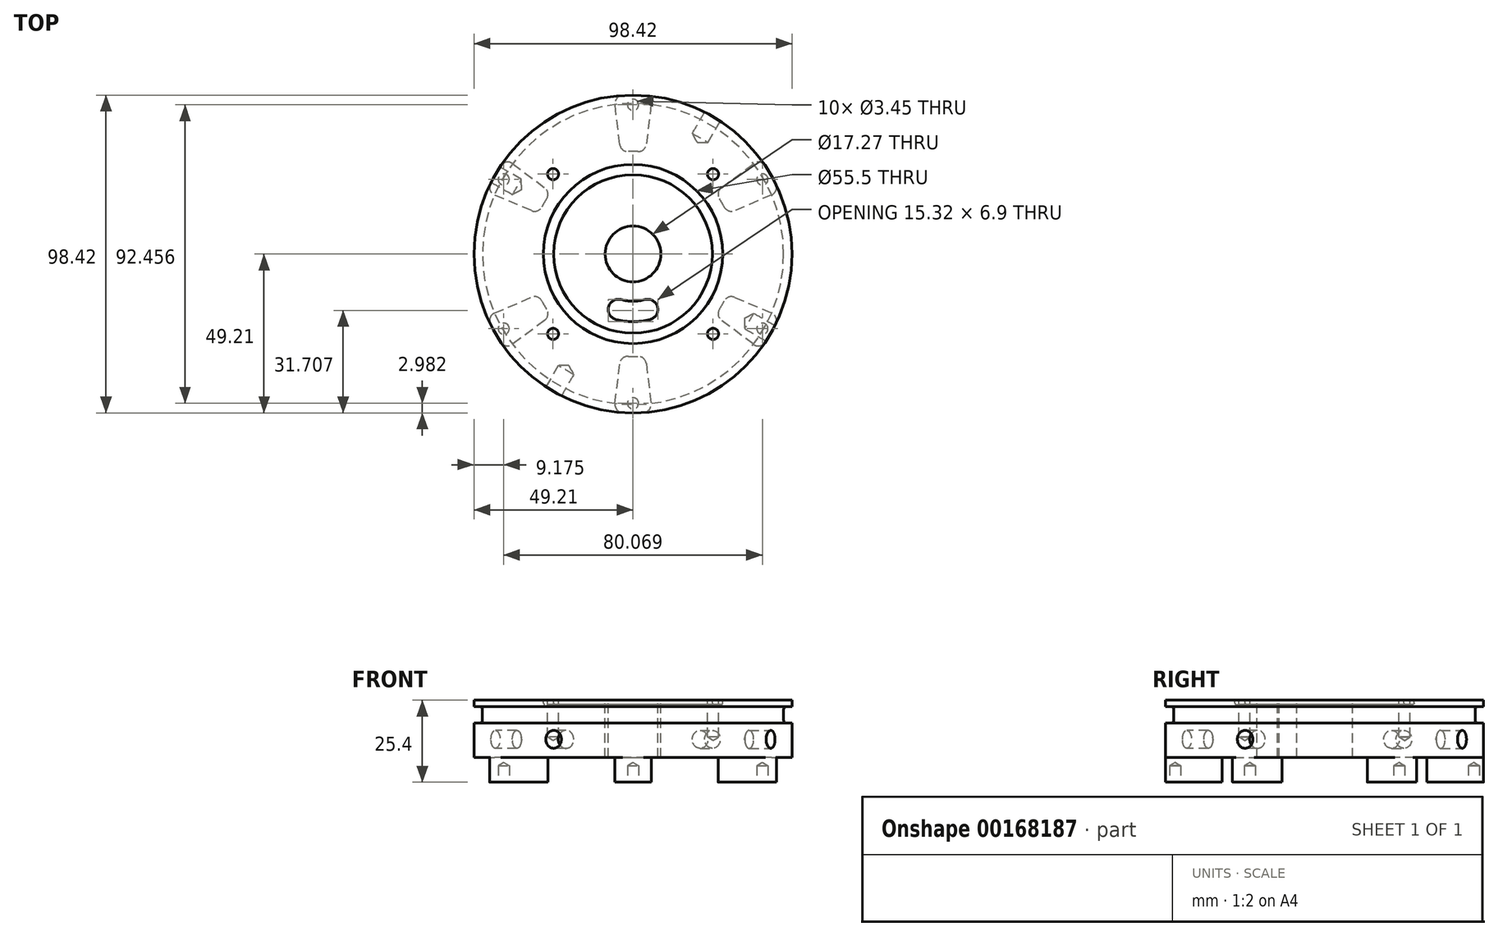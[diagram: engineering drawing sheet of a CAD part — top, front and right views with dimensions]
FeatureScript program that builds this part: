
annotation { "Feature Type Name" : "Feature", "Feature Type Description" : "" }
export const myFeature = defineFeature(function(context is Context, id is Id, definition is map)
    precondition{}
    {
        {
            var Q0;
            Q0=qCreatedBy(makeId("Top.planeOp"),FACE);
            var sketch = newSketch(context, id + "F0", { "sketchPlane" : qUnion([Q0])});
            skCircle(sketch, "E0", {"center": v(0, 0) * mm, "radius": 49.21 * mm});
            skSolve(sketch);
        }
        {
            var Q0;
            Q0=makeQuery(id+"F0.imprint","IMPRINT",FACE,{"disambiguationData":[TD([[makeQuery(id+"F0.imprint","IMPRINT",EDGE,{"derivedFrom":sQuery(id+"F0.wireOp",EDGE,"E0")}),1.0]])]});
            extrude(context, id + "F1", {"entities" : qUnion([Q0]), "depth" : 17.78 * mm});
        }
        {
            var Q0;
            Q0=makeQuery(id+"FNZgXB3MDCEPfWC_1.boolean.opBoolean","SPLIT",FACE,{"disambiguationData":[TD([makeQuery(id+"FNZgXB3MDCEPfWC_1.opExtrude","SWEPT_FACE",FACE,{"disambiguationData":[OSD([sQuery(id+"FiLk9hSRQ8Dv81E_1.wireOp",EDGE,"Xvq2NHEn-EDZK-GzOR-rNrk-moL4fFsD4KvI")])]})])],"derivedFrom":makeQuery(id+"F1.opExtrude","CAP_FACE",FACE,{"disambiguationData":[OSD([sQuery(id+"F0.wireOp",EDGE,"E0")])],"isStart":false})});
            var sketch = newSketch(context, id + "F2", { "sketchPlane" : qUnion([Q0])});
            skCircle(sketch, "E1", {"center": v(0, 0) * mm, "radius": 8.64 * mm});
            skSolve(sketch);
        }
        {
            var Q0;
            Q0=qSketchRegion(id+"F2",true);
            extrude(context, id + "F3", {"entities" : qUnion([Q0]), "operationType" : NewBodyOperationType.REMOVE, "endBound" : BoundingType.THROUGH_ALL, "oppositeDirection" : true, "depth" : 25.4 * mm});
        }
        {
            var Q0;
            Q0=makeQuery(id+"F1.opExtrude","CAP_FACE",FACE,{"disambiguationData":[OSD([sQuery(id+"F0.wireOp",EDGE,"E0")])],"isStart":true});
            var sketch = newSketch(context, id + "F4", { "sketchPlane" : qUnion([Q0])});
            skArc(sketch, "E2", {"start": v(-5.9, -48.86) * mm, "mid": v(0, -49.21) * mm, "end": v(5.9, -48.86) * mm});
            skArc(sketch, "E3", {"start": v(-3.81, -31.52) * mm, "mid": v(0, -31.75) * mm, "end": v(3.8, -31.52) * mm});
            skLineSegment(sketch, "E4", {"start": v(0, 0) * mm, "end": v(3.81, -31.52) * mm, "construction": true});
            skLineSegment(sketch, "E5", {"start": v(5.9, -48.86) * mm, "end": v(3.8, -31.52) * mm});
            skLineSegment(sketch, "E6", {"start": v(-3.8, -31.52) * mm, "end": v(-5.9, -48.86) * mm});
            skLineSegment(sketch, "E7", {"start": v(-3.81, -31.52) * mm, "end": v(3.81, -31.52) * mm, "construction": true});
            skPoint(sketch, "E8", {"position": v(0, -31.52) * mm});
            skLineSegment(sketch, "E9", {"start": v(0, 0) * mm, "end": v(-3.81, -31.52) * mm, "construction": true});
            skSolve(sketch);
        }
        {
            var Q0;
            Q0=qSketchRegion(id+"F4",true);
            extrude(context, id + "F5", {"entities" : qUnion([Q0]), "operationType" : NewBodyOperationType.ADD, "depth" : 7.62 * mm});
        }
        {
            var Q0;
            Q0=makeQuery(id+"F5.opExtrude","SWEPT_EDGE",EDGE,{"disambiguationData":[OSD([sQuery(id+"F0.wireOp",EDGE,"E0"),sQuery(id+"F4.wireOp",EDGE,"E2"),sQuery(id+"F4.wireOp",EDGE,"E5")])]});
            var Q1;
            Q1=makeQuery(id+"F5.opExtrude","SWEPT_EDGE",EDGE,{"disambiguationData":[OSD([sQuery(id+"F4.wireOp",EDGE,"E3"),sQuery(id+"F4.wireOp",EDGE,"E5")])]});
            var Q2;
            Q2=makeQuery(id+"F5.opExtrude","SWEPT_EDGE",EDGE,{"disambiguationData":[OSD([sQuery(id+"F0.wireOp",EDGE,"E0"),sQuery(id+"F4.wireOp",EDGE,"E2"),sQuery(id+"F4.wireOp",EDGE,"sxsrdx0H-xiQs-OsdF-6Z6r-2XBd8uqwUAgb")])]});
            var Q3;
            Q3=makeQuery(id+"F5.opExtrude","SWEPT_EDGE",EDGE,{"disambiguationData":[OSD([sQuery(id+"F4.wireOp",EDGE,"E3"),sQuery(id+"F4.wireOp",EDGE,"sxsrdx0H-xiQs-OsdF-6Z6r-2XBd8uqwUAgb")])]});
            fillet(context, id + "F6", {"entities" : qUnion([Q0, Q1, Q2, Q3]), "radius" : 2.54 * mm, "tangentPropagation" : true, "allowEdgeOverflow" : false});
        }
        {
            var Q0;
            Q0=makeQuery(id+"F5.opExtrude","CAP_FACE",FACE,{"disambiguationData":[OSD([sQuery(id+"F4.wireOp",EDGE,"E2"),sQuery(id+"F4.wireOp",EDGE,"E3"),sQuery(id+"F4.wireOp",EDGE,"E5"),sQuery(id+"F4.wireOp",EDGE,"sxsrdx0H-xiQs-OsdF-6Z6r-2XBd8uqwUAgb")])],"isStart":false});
            var sketch = newSketch(context, id + "F7", { "sketchPlane" : qUnion([Q0])});
            skLineSegment(sketch, "E10", {"start": v(0, 0) * mm, "end": v(0, 0) * mm});
            skLineSegment(sketch, "E11", {"start": v(0, 0) * mm, "end": v(0, -49.1) * mm, "construction": true});
            skPoint(sketch, "E12.3.0", {"position": v(0, -46.23) * mm});
            skPoint(sketch, "E12.center", {"position": v(0, 0) * mm});
            skPoint(sketch, "E13.1.0", {"position": v(40.03, -23.11) * mm});
            skPoint(sketch, "E13.2.0", {"position": v(40.03, 23.11) * mm});
            skPoint(sketch, "E14.0.3.0", {"position": v(0, 46.23) * mm});
            skPoint(sketch, "E14.0.4.0", {"position": v(-40.03, 23.11) * mm});
            skPoint(sketch, "E14.0.5.0", {"position": v(-40.03, -23.11) * mm});
            skSolve(sketch);
        }
        {
            var Q0;
            Q0=makeQuery(id+"F1.opExtrude","SWEPT_BODY",BODY,{"disambiguationData":[OSD([sQuery(id+"F0.wireOp",EDGE,"E0")])]});
            var Q1;
            Q1=makeQuery(id+"F3.boolean.opBoolean","COPY",FACE,{"derivedFrom":makeQuery(id+"F3.opExtrude","SWEPT_FACE",FACE,{"disambiguationData":[OSD([sQuery(id+"F2.wireOp",EDGE,"E1")])]})});
            circularPattern(context, id + "F8", {"operationType" : NewBodyOperationType.ADD, "entities" : qUnion([Q0]), "axis" : qUnion([Q1]), "angle" : 360 * degree, "instanceCount" : 6, "equalSpace" : true});
        }
        {
            var Q0;
            Q0=sQuery(id+"F7.wireOp",VERTEX,"E12.3.0");
            var Q1;
            Q1=sQuery(id+"F7.wireOp",VERTEX,"E13.1.0");
            var Q2;
            Q2=sQuery(id+"F7.wireOp",VERTEX,"E13.2.0");
            var Q3;
            Q3=sQuery(id+"F7.wireOp",VERTEX,"E14.0.3.0");
            var Q4;
            Q4=sQuery(id+"F7.wireOp",VERTEX,"E14.0.4.0");
            var Q5;
            Q5=sQuery(id+"F7.wireOp",VERTEX,"E14.0.5.0");
            var Q6;
            Q6=makeQuery(id+"F1.opExtrude","SWEPT_BODY",BODY,{"disambiguationData":[OSD([sQuery(id+"F0.wireOp",EDGE,"E0")])]});
            hole(context, id + "F9", {"style" : HoleStyle.SIMPLE, "endStyle" : HoleEndStyle.BLIND, "standardTappedOrClearance" : lookupTablePath({ "standard" : "ANSI", "engagement" : "75%", "pitch" : "32 tpi", "size" : "#8", "type" : "Tapped" }), "standardBlindInLast" : lookupTablePath({ "standard" : "ANSI", "engagement" : "75%", "pitch" : "32 tpi", "size" : "#8", "type" : "Tapped" }), "holeDiameter" : 3.45 * mm, "holeDepth" : 5.08 * mm, "locations" : qUnion([Q0, Q1, Q2, Q3, Q4, Q5]), "scope" : qUnion([Q6]), "majorDiameter" : 4.17 * mm});
        }
        {
            var Q0;
            Q0=makeQuery(id+"FkcieFRIapZdHPD_1.boolean.opBoolean","SPLIT",FACE,{"disambiguationData":[TD([makeQuery(id+"F3.boolean.opBoolean","COPY",FACE,{"derivedFrom":makeQuery(id+"F3.opExtrude","SWEPT_FACE",FACE,{"disambiguationData":[OSD([sQuery(id+"F2.wireOp",EDGE,"E1")])]})})])],"derivedFrom":makeQuery(id+"F1.opExtrude","CAP_FACE",FACE,{"disambiguationData":[OSD([sQuery(id+"F0.wireOp",EDGE,"E0")])],"isStart":false})});
            var sketch = newSketch(context, id + "F10", { "sketchPlane" : qUnion([Q0])});
            skCircle(sketch, "E15", {"center": v(0, 0) * mm, "radius": 26.15 * mm, "construction": true});
            skCircle(sketch, "E16", {"center": v(0, 0) * mm, "radius": 24.55 * mm});
            skCircle(sketch, "E17", {"center": v(0, 0) * mm, "radius": 27.75 * mm});
            skSolve(sketch);
        }
        {
            var Q0;
            Q0=qSketchRegion(id+"F10",true);
            extrude(context, id + "F11", {"entities" : qUnion([Q0]), "operationType" : NewBodyOperationType.REMOVE, "oppositeDirection" : true, "depth" : 1.3 * mm});
        }
        {
            var Q0;
            Q0=makeQuery(id+"F11.boolean.opBoolean","COPY",EDGE,{"derivedFrom":makeQuery(id+"F11.opExtrude","CAP_EDGE",EDGE,{"disambiguationData":[OSD([sQuery(id+"F10.wireOp",EDGE,"E17")])],"isStart":false})});
            var Q1;
            Q1=makeQuery(id+"F11.boolean.opBoolean","COPY",EDGE,{"derivedFrom":makeQuery(id+"F11.opExtrude","CAP_EDGE",EDGE,{"disambiguationData":[OSD([sQuery(id+"F10.wireOp",EDGE,"E16")])],"isStart":false})});
            fillet(context, id + "F12", {"entities" : qUnion([Q0, Q1]), "radius" : 0.4 * mm, "tangentPropagation" : true, "allowEdgeOverflow" : false});
        }
        {
            var Q0;
            {var subQ0=makeQuery(id+"F3.boolean.opBoolean","COPY",FACE,{"derivedFrom":makeQuery(id+"F3.opExtrude","SWEPT_FACE",FACE,{"disambiguationData":[OSD([sQuery(id+"F2.wireOp",EDGE,"E1")])]})});Q0=makeQuery(id+"F11.boolean.opBoolean","SPLIT",FACE,{"disambiguationData":[TD([subQ0])],"derivedFrom":makeQuery(id+"FkcieFRIapZdHPD_1.boolean.opBoolean","SPLIT",FACE,{"disambiguationData":[TD([subQ0])],"derivedFrom":makeQuery(id+"F1.opExtrude","CAP_FACE",FACE,{"disambiguationData":[OSD([sQuery(id+"F0.wireOp",EDGE,"E0")])],"isStart":false})})});}
            var sketch = newSketch(context, id + "F13", { "sketchPlane" : qUnion([Q0])});
            skLineSegment(sketch, "E18", {"start": v(0, 0) * mm, "end": v(6.17, -13.24) * mm, "construction": true});
            skArc(sketch, "E19", {"start": v(6.17, -13.24) * mm, "mid": v(0, -14.6) * mm, "end": v(-6.17, -13.24) * mm});
            skArc(sketch, "E20", {"start": v(8.86, -19) * mm, "mid": v(0, -20.95) * mm, "end": v(-8.86, -19) * mm});
            skLineSegment(sketch, "E21", {"start": v(-8.86, -19) * mm, "end": v(-6.17, -13.24) * mm});
            skLineSegment(sketch, "E22", {"start": v(0, 0) * mm, "end": v(-6.17, -13.24) * mm, "construction": true});
            skLineSegment(sketch, "E23", {"start": v(8.86, -19) * mm, "end": v(6.17, -13.24) * mm});
            skLineSegment(sketch, "E24", {"start": v(0, -14.6) * mm, "end": v(0, 0) * mm, "construction": true});
            skPoint(sketch, "E25", {"position": v(-7.51, -16.11) * mm});
            skSolve(sketch);
        }
        {
            var Q0;
            Q0=qSketchRegion(id+"F13",true);
            extrude(context, id + "F14", {"entities" : qUnion([Q0]), "operationType" : NewBodyOperationType.REMOVE, "endBound" : BoundingType.THROUGH_ALL, "oppositeDirection" : true, "depth" : 25.4 * mm});
        }
        {
            var Q0;
            Q0=makeQuery(id+"F14.boolean.opBoolean","COPY",EDGE,{"derivedFrom":makeQuery(id+"F14.opExtrude","SWEPT_EDGE",EDGE,{"disambiguationData":[OSD([sQuery(id+"F13.wireOp",EDGE,"E19"),sQuery(id+"F13.wireOp",EDGE,"E21")])]})});
            var Q1;
            Q1=makeQuery(id+"F14.boolean.opBoolean","COPY",EDGE,{"derivedFrom":makeQuery(id+"F14.opExtrude","SWEPT_EDGE",EDGE,{"disambiguationData":[OSD([sQuery(id+"F13.wireOp",EDGE,"E20"),sQuery(id+"F13.wireOp",EDGE,"E21")])]})});
            var Q2;
            Q2=makeQuery(id+"F14.boolean.opBoolean","COPY",EDGE,{"derivedFrom":makeQuery(id+"F14.opExtrude","SWEPT_EDGE",EDGE,{"disambiguationData":[OSD([sQuery(id+"F13.wireOp",EDGE,"E19"),sQuery(id+"F13.wireOp",EDGE,"nJm0js4g-YAOA-XNub-Ppl5-B8IrQimasCNu")])]})});
            var Q3;
            Q3=makeQuery(id+"F14.boolean.opBoolean","COPY",EDGE,{"derivedFrom":makeQuery(id+"F14.opExtrude","SWEPT_EDGE",EDGE,{"disambiguationData":[OSD([sQuery(id+"F13.wireOp",EDGE,"E20"),sQuery(id+"F13.wireOp",EDGE,"nJm0js4g-YAOA-XNub-Ppl5-B8IrQimasCNu")])]})});
            fillet(context, id + "F15", {"entities" : qUnion([Q0, Q1, Q2, Q3]), "radius" : 3.17 * mm, "tangentPropagation" : true, "allowEdgeOverflow" : false});
        }
        {
            var Q0;
            {var subQ0=makeQuery(id+"F3.boolean.opBoolean","COPY",FACE,{"derivedFrom":makeQuery(id+"F3.opExtrude","SWEPT_FACE",FACE,{"disambiguationData":[OSD([sQuery(id+"F2.wireOp",EDGE,"E1")])]})});Q0=makeQuery(id+"F11.boolean.opBoolean","SPLIT",FACE,{"disambiguationData":[TD([subQ0])],"derivedFrom":makeQuery(id+"FkcieFRIapZdHPD_1.boolean.opBoolean","SPLIT",FACE,{"disambiguationData":[TD([subQ0])],"derivedFrom":makeQuery(id+"F1.opExtrude","CAP_FACE",FACE,{"disambiguationData":[OSD([sQuery(id+"F0.wireOp",EDGE,"E0")])],"isStart":false})})});}
            var sketch = newSketch(context, id + "F16", { "sketchPlane" : qUnion([Q0])});
            skCircle(sketch, "E26", {"center": v(0, 0) * mm, "radius": 35 * mm, "construction": true});
            skLineSegment(sketch, "E27", {"start": v(0, 0) * mm, "end": v(35, 0) * mm, "construction": true});
            skPoint(sketch, "E28", {"position": v(35, 0) * mm});
            skLineSegment(sketch, "E29", {"start": v(0, 0) * mm, "end": v(24.75, -24.75) * mm, "construction": true});
            skPoint(sketch, "E30", {"position": v(24.75, -24.75) * mm});
            skPoint(sketch, "E31.1.0", {"position": v(24.75, 24.75) * mm});
            skPoint(sketch, "E31.2.0", {"position": v(-24.75, 24.75) * mm});
            skPoint(sketch, "E31.3.0", {"position": v(-24.75, -24.75) * mm});
            skSolve(sketch);
        }
        {
            var Q0;
            Q0=sQuery(id+"F16.wireOp",VERTEX,"E30");
            var Q1;
            Q1=sQuery(id+"F16.wireOp",VERTEX,"E31.3.0");
            var Q2;
            Q2=sQuery(id+"F16.wireOp",VERTEX,"E31.2.0");
            var Q3;
            Q3=sQuery(id+"F16.wireOp",VERTEX,"E31.1.0");
            var Q4;
            Q4=makeQuery(id+"F1.opExtrude","SWEPT_BODY",BODY,{"disambiguationData":[OSD([sQuery(id+"F0.wireOp",EDGE,"E0")])]});
            hole(context, id + "F17", {"style" : HoleStyle.SIMPLE, "endStyle" : HoleEndStyle.BLIND, "standardTappedOrClearance" : lookupTablePath({ "standard" : "ANSI", "engagement" : "75%", "pitch" : "32 tpi", "size" : "#8", "type" : "Tapped" }), "standardBlindInLast" : lookupTablePath({ "standard" : "ANSI", "engagement" : "75%", "pitch" : "32 tpi", "size" : "#8", "type" : "Tapped" }), "holeDiameter" : 3.45 * mm, "holeDepth" : 11.43 * mm, "locations" : qUnion([Q0, Q1, Q2, Q3]), "scope" : qUnion([Q4]), "majorDiameter" : 4.17 * mm});
        }
        {
            var Q0;
            Q0=makeQuery(id+"F11.boolean.opBoolean","SPLIT",FACE,{"disambiguationData":[TD([makeQuery(id+"F3.boolean.opBoolean","COPY",FACE,{"derivedFrom":makeQuery(id+"F3.opExtrude","SWEPT_FACE",FACE,{"disambiguationData":[OSD([sQuery(id+"F2.wireOp",EDGE,"E1")])]})})])],"derivedFrom":makeQuery(id+"F1.opExtrude","CAP_FACE",FACE,{"disambiguationData":[OSD([sQuery(id+"F0.wireOp",EDGE,"E0")])],"isStart":false})});
            cPlane(context, id + "F18", {"entities" : qUnion([Q0]), "cplaneType" : CPlaneType.OFFSET, "offset" : 2.03 * mm, "oppositeDirection" : true, "width" : 152.4 * mm, "height" : 152.4 * mm});
        }
        {
            var Q0;
            Q0=qCreatedBy(id+"F18.planeOp",FACE);
            var sketch = newSketch(context, id + "F19", { "sketchPlane" : qUnion([Q0])});
            skCircle(sketch, "E32", {"center": v(0, 0) * mm, "radius": 46.62 * mm});
            skCircle(sketch, "E33.0", {"center": v(0, 0) * mm, "radius": 49.21 * mm});
            skSolve(sketch);
        }
        {
            var Q0;
            Q0=qSketchRegion(id+"F19",true);
            extrude(context, id + "F20", {"entities" : qUnion([Q0]), "operationType" : NewBodyOperationType.REMOVE, "oppositeDirection" : true, "depth" : 5 * mm});
        }
        {
            var Q0;
            Q0=makeQuery(id+"F20.boolean.opBoolean","COPY",EDGE,{"derivedFrom":makeQuery(id+"F20.opExtrude","CAP_EDGE",EDGE,{"disambiguationData":[OSD([sQuery(id+"F19.wireOp",EDGE,"E32")])],"isStart":false})});
            var Q1;
            Q1=makeQuery(id+"F20.boolean.opBoolean","COPY",EDGE,{"derivedFrom":makeQuery(id+"F20.opExtrude","CAP_EDGE",EDGE,{"disambiguationData":[OSD([sQuery(id+"F19.wireOp",EDGE,"E32")])],"isStart":true})});
            fillet(context, id + "F21", {"entities" : qUnion([Q0, Q1]), "radius" : 0.76 * mm, "tangentPropagation" : true, "allowEdgeOverflow" : false});
        }
        {
            var Q0;
            {var subQ1=sQuery(id+"F0.wireOp",EDGE,"E0");var subQ2=makeQuery(id+"F1.opExtrude","SWEPT_FACE",FACE,{"disambiguationData":[OSD([subQ1])]});Q0=makeQuery(id+"FkcieFRIapZdHPD_1.boolean.opBoolean","SPLIT",FACE,{"disambiguationData":[TD([subQ2])],"derivedFrom":makeQuery(id+"F1.opExtrude","CAP_FACE",FACE,{"disambiguationData":[OSD([subQ1])],"isStart":false})});}
            var sketch = newSketch(context, id + "F22", { "sketchPlane" : qUnion([Q0])});
            skCircle(sketch, "E34.0", {"center": v(0, 0) * mm, "radius": 49.21 * mm, "construction": true});
            skPoint(sketch, "E35", {"position": v(-24.6, -42.62) * mm});
            skLineSegment(sketch, "E36", {"start": v(0, -49.21) * mm, "end": v(0, 0) * mm, "construction": true});
            skLineSegment(sketch, "E37", {"start": v(0, 0) * mm, "end": v(-17.96, -31.1) * mm, "construction": true});
            skLineSegment(sketch, "E38", {"start": v(-17.96, -31.1) * mm, "end": v(-24.6, -42.62) * mm, "construction": true});
            skLineSegment(sketch, "E39", {"start": v(0, 0) * mm, "end": v(24.6, 42.62) * mm, "construction": true});
            skLineSegment(sketch, "E40", {"start": v(24.6, 42.62) * mm, "end": v(0, 0) * mm, "construction": true});
            skLineSegment(sketch, "E41", {"start": v(42.62, -24.6) * mm, "end": v(0, 0) * mm, "construction": true});
            skLineSegment(sketch, "E42", {"start": v(0, 0) * mm, "end": v(-42.62, 24.6) * mm, "construction": true});
            skPoint(sketch, "E43", {"position": v(24.6, 42.62) * mm});
            skPoint(sketch, "E44", {"position": v(42.62, -24.6) * mm});
            skPoint(sketch, "E45", {"position": v(-42.62, 24.6) * mm});
            skSolve(sketch);
        }
        {
            var Q0;
            Q0=qCreatedBy(makeId("Front.planeOp"),FACE);
            var sketch = newSketch(context, id + "F23", { "sketchPlane" : qUnion([Q0])});
            skLineSegment(sketch, "E46", {"start": v(0, 0) * mm, "end": v(0, 38.57) * mm, "construction": true});
            skSolve(sketch);
        }
        {
            var Q0;
            Q0=sQuery(id+"F23.wireOp",EDGE,"E46");
            cPlane(context, id + "F24", {"entities" : qUnion([Q0]), "cplaneType" : CPlaneType.LINE_ANGLE, "offset" : 25.4 * mm, "angle" : 60 * degree, "width" : 152.4 * mm, "height" : 152.4 * mm});
        }
        {
            var Q0;
            Q0=sQuery(id+"F22.wireOp",VERTEX,"E35");
            var Q1;
            Q1=qCreatedBy(id+"F24.planeOp",FACE);
            cPlane(context, id + "F25", {"entities" : qUnion([Q0, Q1]), "cplaneType" : CPlaneType.PLANE_POINT, "offset" : 25.4 * mm, "width" : 152.4 * mm, "height" : 152.4 * mm});
        }
        {
            var Q0;
            Q0=qCreatedBy(id+"F25.planeOp",FACE);
            var Q1;
            Q1=sQuery(id+"F22.wireOp",VERTEX,"E43");
            cPlane(context, id + "F26", {"entities" : qUnion([Q0, Q1]), "cplaneType" : CPlaneType.PLANE_POINT, "offset" : 25.4 * mm, "width" : 152.4 * mm, "height" : 152.4 * mm});
        }
        {
            var Q0;
            Q0=sQuery(id+"F23.wireOp",EDGE,"E46");
            cPlane(context, id + "F27", {"entities" : qUnion([Q0]), "cplaneType" : CPlaneType.LINE_ANGLE, "offset" : 25.4 * mm, "angle" : 150 * degree, "width" : 152.4 * mm, "height" : 152.4 * mm});
        }
        {
            var Q0;
            Q0=sQuery(id+"F22.wireOp",VERTEX,"E45");
            var Q1;
            Q1=qCreatedBy(id+"F27.planeOp",FACE);
            cPlane(context, id + "F28", {"entities" : qUnion([Q0, Q1]), "cplaneType" : CPlaneType.PLANE_POINT, "offset" : 25.4 * mm, "width" : 152.4 * mm, "height" : 152.4 * mm});
        }
        {
            var Q0;
            Q0=qCreatedBy(id+"F27.planeOp",FACE);
            var Q1;
            Q1=sQuery(id+"F22.wireOp",VERTEX,"E44");
            cPlane(context, id + "F29", {"entities" : qUnion([Q0, Q1]), "cplaneType" : CPlaneType.PLANE_POINT, "offset" : 25.4 * mm, "width" : 152.4 * mm, "height" : 152.4 * mm});
        }
        {
            var Q0;
            Q0=qCreatedBy(id+"F25.planeOp",FACE);
            var sketch = newSketch(context, id + "F30", { "sketchPlane" : qUnion([Q0])});
            skLineSegment(sketch, "E47", {"start": v(0, 0) * mm, "end": v(0, 5.66) * mm, "construction": true});
            skPoint(sketch, "E48", {"position": v(0, 5.66) * mm});
            skSolve(sketch);
        }
        {
            var Q0;
            Q0=qCreatedBy(id+"F26.planeOp",FACE);
            var sketch = newSketch(context, id + "F31", { "sketchPlane" : qUnion([Q0])});
            skPoint(sketch, "E49", {"position": v(0, 5.66) * mm});
            skLineSegment(sketch, "E50.0", {"start": v(0, 0) * mm, "end": v(0, 5.66) * mm, "construction": true});
            skSolve(sketch);
        }
        {
            var Q0;
            Q0=qCreatedBy(id+"F28.planeOp",FACE);
            var sketch = newSketch(context, id + "F32", { "sketchPlane" : qUnion([Q0])});
            skLineSegment(sketch, "E51", {"start": v(0, 0) * mm, "end": v(0, 5.66) * mm, "construction": true});
            skLineSegment(sketch, "E52.0", {"start": v(-49.21, 0) * mm, "end": v(-49.21, 5.66) * mm, "construction": true});
            skPoint(sketch, "E53", {"position": v(0, 5.66) * mm});
            skLineSegment(sketch, "E54", {"start": v(-49.21, 5.66) * mm, "end": v(0, 5.66) * mm, "construction": true});
            skSolve(sketch);
        }
        {
            var Q0;
            Q0=qCreatedBy(id+"F29.planeOp",FACE);
            var sketch = newSketch(context, id + "F33", { "sketchPlane" : qUnion([Q0])});
            skLineSegment(sketch, "E55.0", {"start": v(0, 0) * mm, "end": v(0, 5.66) * mm, "construction": true});
            skPoint(sketch, "E56", {"position": v(0, 5.66) * mm});
            skSolve(sketch);
        }
        {
            var Q0;
            Q0=sQuery(id+"F33.wireOp",VERTEX,"E56");
            var Q1;
            Q1=makeQuery(id+"F1.opExtrude","SWEPT_BODY",BODY,{"disambiguationData":[OSD([sQuery(id+"F0.wireOp",EDGE,"E0")])]});
            hole(context, id + "F34", {"style" : HoleStyle.SIMPLE, "endStyle" : HoleEndStyle.BLIND, "oppositeDirection" : true, "standardTappedOrClearance" : lookupTablePath({ "standard" : "ANSI", "engagement" : "75%", "pitch" : "32 tpi", "size" : "1/4", "type" : "Tapped" }), "standardBlindInLast" : lookupTablePath({ "standard" : "ANSI", "engagement" : "75%", "pitch" : "32 tpi", "size" : "1/4", "type" : "Tapped" }), "holeDiameter" : 5.56 * mm, "holeDepth" : 7.62 * mm, "locations" : qUnion([Q0]), "scope" : qUnion([Q1]), "majorDiameter" : 6.35 * mm});
        }
        {
            var Q0;
            Q0=sQuery(id+"F32.wireOp",VERTEX,"E53");
            var Q1;
            Q1=makeQuery(id+"F1.opExtrude","SWEPT_BODY",BODY,{"disambiguationData":[OSD([sQuery(id+"F0.wireOp",EDGE,"E0")])]});
            hole(context, id + "F35", {"style" : HoleStyle.SIMPLE, "endStyle" : HoleEndStyle.BLIND, "standardTappedOrClearance" : lookupTablePath({ "standard" : "ANSI", "engagement" : "75%", "pitch" : "32 tpi", "size" : "1/4", "type" : "Tapped" }), "standardBlindInLast" : lookupTablePath({ "standard" : "ANSI", "engagement" : "75%", "pitch" : "32 tpi", "size" : "1/4", "type" : "Tapped" }), "holeDiameter" : 5.56 * mm, "holeDepth" : 7.62 * mm, "locations" : qUnion([Q0]), "scope" : qUnion([Q1]), "majorDiameter" : 6.35 * mm});
        }
        {
            var Q0;
            Q0=sQuery(id+"F30.wireOp",VERTEX,"E48");
            var Q1;
            Q1=makeQuery(id+"F1.opExtrude","SWEPT_BODY",BODY,{"disambiguationData":[OSD([sQuery(id+"F0.wireOp",EDGE,"E0")])]});
            hole(context, id + "F36", {"style" : HoleStyle.SIMPLE, "endStyle" : HoleEndStyle.BLIND, "oppositeDirection" : true, "standardTappedOrClearance" : lookupTablePath({ "standard" : "ANSI", "engagement" : "75%", "pitch" : "32 tpi", "size" : "1/4", "type" : "Tapped" }), "standardBlindInLast" : lookupTablePath({ "standard" : "ANSI", "engagement" : "75%", "pitch" : "32 tpi", "size" : "1/4", "type" : "Tapped" }), "holeDiameter" : 5.56 * mm, "holeDepth" : 7.62 * mm, "locations" : qUnion([Q0]), "scope" : qUnion([Q1]), "majorDiameter" : 6.35 * mm});
        }
        {
            var Q0;
            Q0=sQuery(id+"F31.wireOp",VERTEX,"E49");
            var Q1;
            Q1=makeQuery(id+"F1.opExtrude","SWEPT_BODY",BODY,{"disambiguationData":[OSD([sQuery(id+"F0.wireOp",EDGE,"E0")])]});
            hole(context, id + "F37", {"style" : HoleStyle.SIMPLE, "endStyle" : HoleEndStyle.BLIND, "standardTappedOrClearance" : lookupTablePath({ "standard" : "ANSI", "engagement" : "75%", "pitch" : "32 tpi", "size" : "1/4", "type" : "Tapped" }), "standardBlindInLast" : lookupTablePath({ "standard" : "ANSI", "engagement" : "75%", "pitch" : "32 tpi", "size" : "1/4", "type" : "Tapped" }), "holeDiameter" : 5.56 * mm, "holeDepth" : 7.62 * mm, "locations" : qUnion([Q0]), "scope" : qUnion([Q1]), "majorDiameter" : 6.35 * mm});
        }
    });
